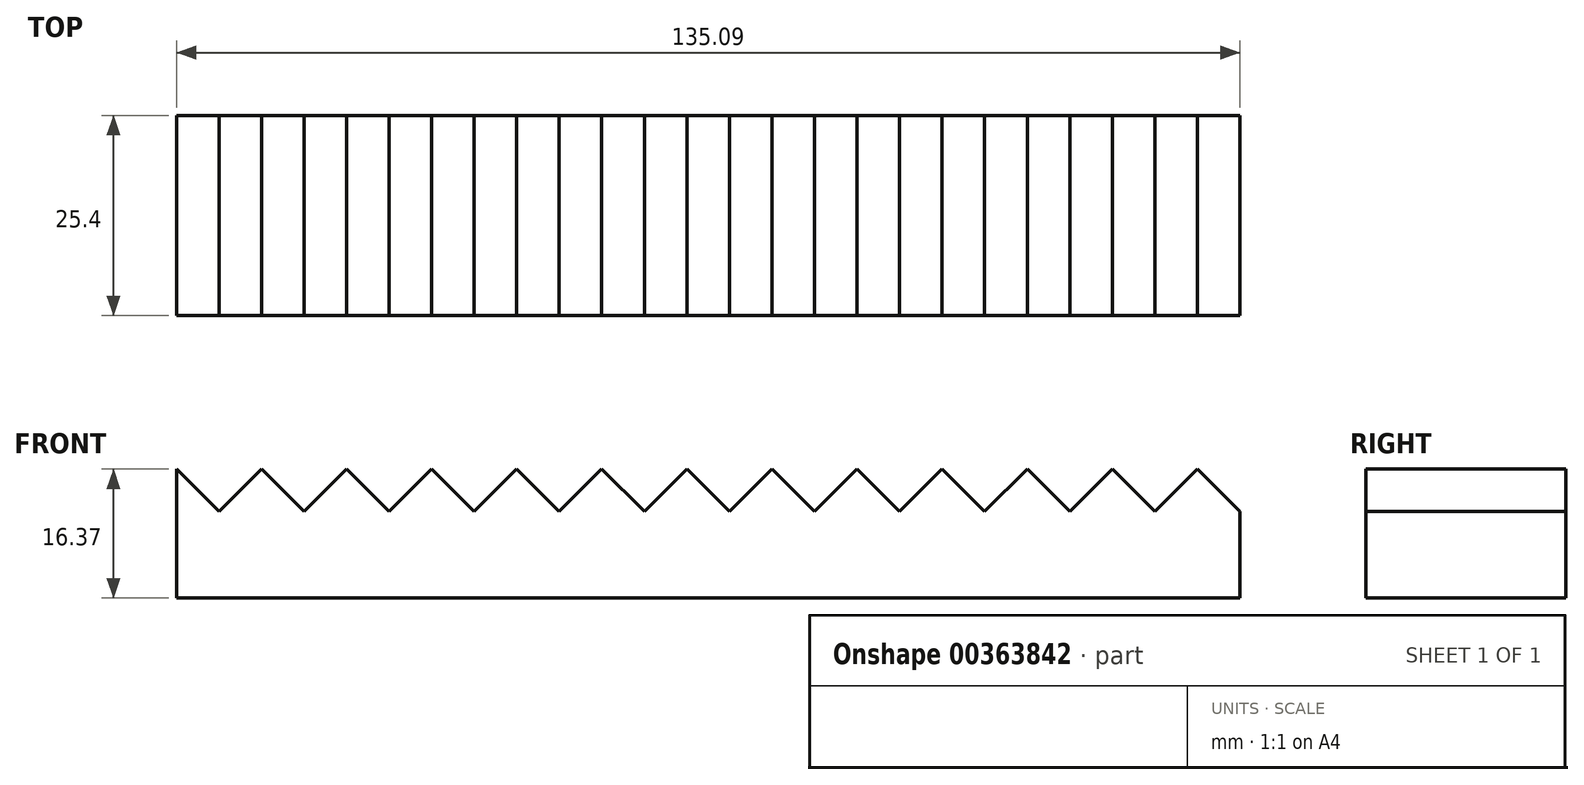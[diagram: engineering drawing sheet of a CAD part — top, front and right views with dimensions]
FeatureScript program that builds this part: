
annotation { "Feature Type Name" : "Feature", "Feature Type Description" : "" }
export const myFeature = defineFeature(function(context is Context, id is Id, definition is map)
    precondition{}
    {
        {
            var Q0;
            Q0=qCreatedBy(makeId("Front.planeOp"),FACE);
            var sketch = newSketch(context, id + "F0", { "sketchPlane" : qUnion([Q0])});
            skLineSegment(sketch, "E0", {"start": v(-73.43, -16.37) * mm, "end": v(61.66, -16.37) * mm});
            skLineSegment(sketch, "E1", {"start": v(61.66, -16.37) * mm, "end": v(61.66, 0) * mm});
            skLineSegment(sketch, "E2", {"start": v(-73.43, -16.37) * mm, "end": v(-73.43, 0) * mm});
            skLineSegment(sketch, "E3", {"start": v(-73.43, 0) * mm, "end": v(-68.03, -5.4) * mm});
            skLineSegment(sketch, "E4", {"start": v(-68.03, -5.4) * mm, "end": v(-62.63, 0) * mm});
            skLineSegment(sketch, "E5", {"start": v(-62.63, 0) * mm, "end": v(-57.22, -5.4) * mm});
            skLineSegment(sketch, "E6", {"start": v(-57.22, -5.4) * mm, "end": v(-51.82, 0) * mm});
            skLineSegment(sketch, "E7", {"start": v(-51.82, 0) * mm, "end": v(-46.41, -5.4) * mm});
            skLineSegment(sketch, "E8", {"start": v(-46.41, -5.4) * mm, "end": v(-41, 0) * mm});
            skLineSegment(sketch, "E9", {"start": v(-41, 0) * mm, "end": v(-35.6, -5.4) * mm});
            skLineSegment(sketch, "E10", {"start": v(-35.6, -5.4) * mm, "end": v(-30.2, 0) * mm});
            skLineSegment(sketch, "E11", {"start": v(-30.2, 0) * mm, "end": v(-24.8, -5.4) * mm});
            skLineSegment(sketch, "E12", {"start": v(-24.8, -5.4) * mm, "end": v(-19.4, 0) * mm});
            skLineSegment(sketch, "E13", {"start": v(-19.4, 0) * mm, "end": v(-14, -5.4) * mm});
            skLineSegment(sketch, "E14", {"start": v(-14, -5.4) * mm, "end": v(-8.59, 0) * mm});
            skLineSegment(sketch, "E15", {"start": v(-8.59, 0) * mm, "end": v(-3.18, -5.4) * mm});
            skLineSegment(sketch, "E16", {"start": v(-3.18, -5.4) * mm, "end": v(2.22, 0) * mm});
            skLineSegment(sketch, "E17", {"start": v(2.22, 0) * mm, "end": v(7.62, -5.4) * mm});
            skLineSegment(sketch, "E18", {"start": v(7.62, -5.4) * mm, "end": v(13.03, 0) * mm});
            skLineSegment(sketch, "E19", {"start": v(13.03, 0) * mm, "end": v(18.43, -5.4) * mm});
            skLineSegment(sketch, "E20", {"start": v(18.43, -5.4) * mm, "end": v(23.84, 0) * mm});
            skLineSegment(sketch, "E21", {"start": v(23.84, 0) * mm, "end": v(29.24, -5.4) * mm});
            skLineSegment(sketch, "E22", {"start": v(29.24, -5.4) * mm, "end": v(34.64, 0) * mm});
            skLineSegment(sketch, "E23", {"start": v(34.64, 0) * mm, "end": v(40.05, -5.4) * mm});
            skLineSegment(sketch, "E24", {"start": v(40.05, -5.4) * mm, "end": v(45.45, 0) * mm});
            skLineSegment(sketch, "E25", {"start": v(45.45, 0) * mm, "end": v(50.85, -5.4) * mm});
            skLineSegment(sketch, "E26", {"start": v(50.85, -5.4) * mm, "end": v(56.26, 0) * mm});
            skLineSegment(sketch, "E27", {"start": v(56.26, 0) * mm, "end": v(61.66, -5.4) * mm});
            skSolve(sketch);
        }
        {
            var Q0;
            Q0 = qSketchRegion(id + "F0", true);
            extrude(context, id + "F1", {"entities" : qUnion([Q0]), "depth" : 25.4 * mm});
        }
    });
